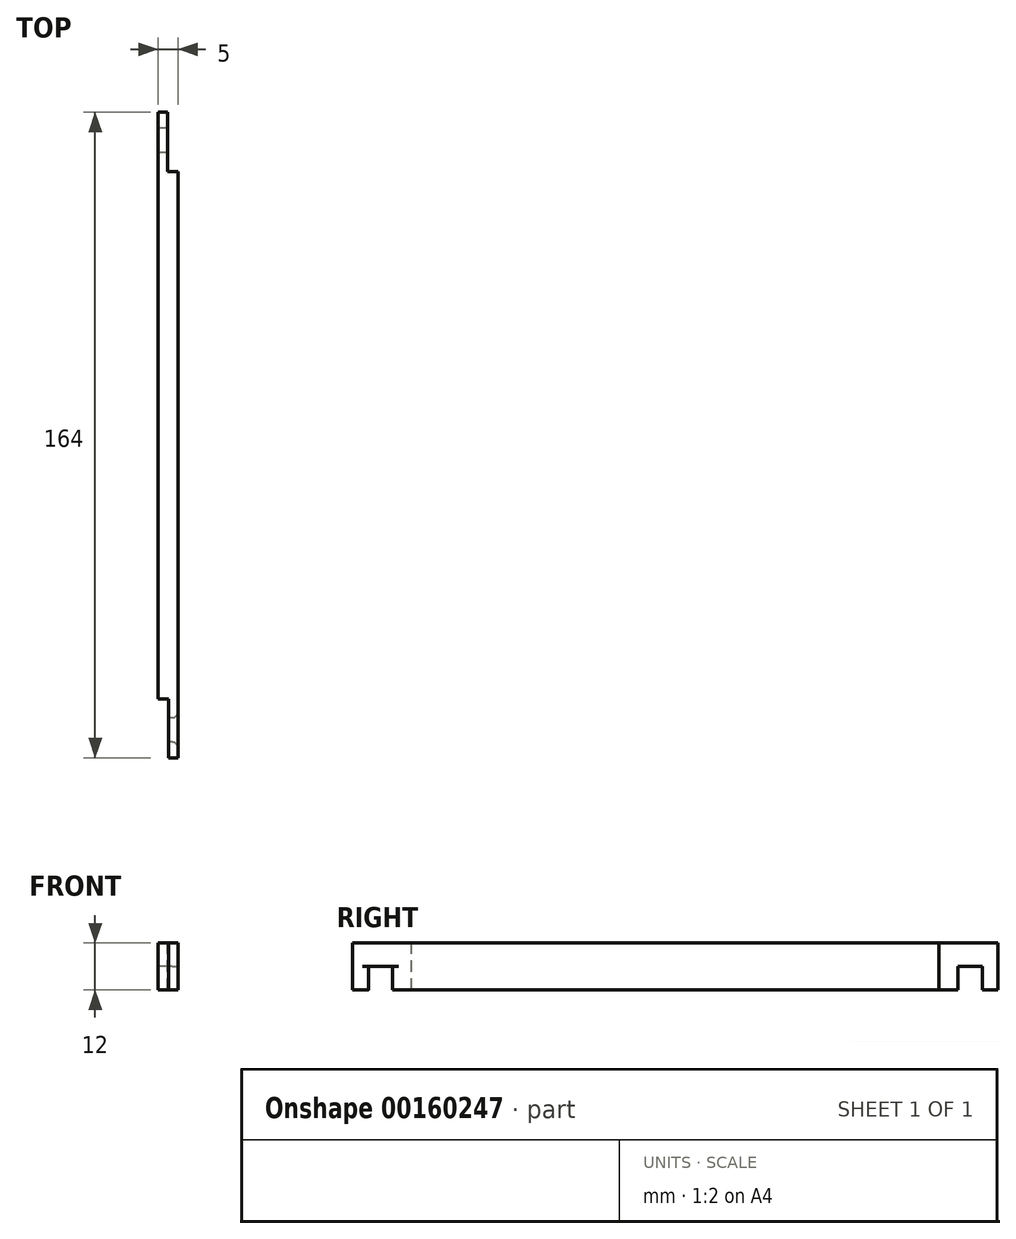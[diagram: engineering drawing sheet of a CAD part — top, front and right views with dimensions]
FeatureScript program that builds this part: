
annotation { "Feature Type Name" : "Feature", "Feature Type Description" : "" }
export const myFeature = defineFeature(function(context is Context, id is Id, definition is map)
    precondition{}
    {
        {
            var Q0;
            Q0=qCreatedBy(makeId("Right.planeOp"),FACE);
            var sketch = newSketch(context, id + "F0", { "sketchPlane" : qUnion([Q0])});
            skLineSegment(sketch, "E0.bottom", {"start": v(-59.21, 0) * mm, "end": v(104.79, 0) * mm});
            skLineSegment(sketch, "E0.top", {"start": v(-59.21, 12) * mm, "end": v(104.79, 12) * mm});
            skLineSegment(sketch, "E0.left", {"start": v(-59.21, 0) * mm, "end": v(-59.21, 12) * mm});
            skLineSegment(sketch, "E0.right", {"start": v(104.79, 0) * mm, "end": v(104.79, 12) * mm});
            skLineSegment(sketch, "E1.bottom", {"start": v(-55.21, 0) * mm, "end": v(-49.01, 0) * mm});
            skLineSegment(sketch, "E1.top", {"start": v(-55.21, 6) * mm, "end": v(-49.01, 6) * mm});
            skLineSegment(sketch, "E1.left", {"start": v(-55.21, 0) * mm, "end": v(-55.21, 6) * mm});
            skLineSegment(sketch, "E1.right", {"start": v(-49.01, 0) * mm, "end": v(-49.01, 6) * mm});
            skLineSegment(sketch, "E2.bottom", {"start": v(100.79, 0) * mm, "end": v(94.59, 0) * mm});
            skLineSegment(sketch, "E2.top", {"start": v(100.79, 6) * mm, "end": v(94.59, 6) * mm});
            skLineSegment(sketch, "E2.left", {"start": v(100.79, 0) * mm, "end": v(100.79, 6) * mm});
            skLineSegment(sketch, "E2.right", {"start": v(94.59, 0) * mm, "end": v(94.59, 6) * mm});
            skSolve(sketch);
        }
        {
            var Q0;
            Q0=makeQuery(id+"F0.imprint","IMPRINT",FACE,{"disambiguationData":[TD([[makeQuery(id+"F0.imprint","IMPRINT",EDGE,{"derivedFrom":sQuery(id+"F0.wireOp",EDGE,"E0.top")}),-1.0]])]});
            extrude(context, id + "F1", {"entities" : qUnion([Q0]), "depth" : 5 * mm});
        }
        {
            var Q0;
            Q0=makeQuery(id+"F1.opExtrude","CAP_EDGE",EDGE,{"disambiguationData":[OSD([sQuery(id+"F0.wireOp",EDGE,"E1.left")])],"isStart":false});
            var Q1;
            Q1=makeQuery(id+"F1.opExtrude","CAP_EDGE",EDGE,{"disambiguationData":[OSD([sQuery(id+"F0.wireOp",EDGE,"E1.right")])],"isStart":false});
            fillet(context, id + "F2", {"entities" : qUnion([Q0, Q1]), "radius" : 1.5 * mm, "tangentPropagation" : true, "allowEdgeOverflow" : false});
        }
        {
            var Q0;
            Q0=makeQuery(id+"F1.opExtrude","SWEPT_FACE",FACE,{"disambiguationData":[OSD([sQuery(id+"F0.wireOp",EDGE,"E0.top")])]});
            var sketch = newSketch(context, id + "F3", { "sketchPlane" : qUnion([Q0])});
            skLineSegment(sketch, "E3.bottom", {"start": v(0, -44.21) * mm, "end": v(2.6, -44.21) * mm});
            skLineSegment(sketch, "E3.top", {"start": v(0, -59.21) * mm, "end": v(2.6, -59.21) * mm});
            skLineSegment(sketch, "E3.left", {"start": v(0, -44.21) * mm, "end": v(0, -59.21) * mm});
            skLineSegment(sketch, "E3.right", {"start": v(2.6, -44.21) * mm, "end": v(2.6, -59.21) * mm});
            skLineSegment(sketch, "E4.bottom", {"start": v(5, 104.79) * mm, "end": v(2.4, 104.79) * mm});
            skLineSegment(sketch, "E4.top", {"start": v(5, 89.79) * mm, "end": v(2.4, 89.79) * mm});
            skLineSegment(sketch, "E4.left", {"start": v(5, 104.79) * mm, "end": v(5, 89.79) * mm});
            skLineSegment(sketch, "E4.right", {"start": v(2.4, 104.79) * mm, "end": v(2.4, 89.79) * mm});
            skSolve(sketch);
        }
        {
            var Q0;
            Q0=makeQuery(id+"F3.imprint","IMPRINT",FACE,{"disambiguationData":[TD([[makeQuery(id+"F3.imprint","IMPRINT",EDGE,{"derivedFrom":sQuery(id+"F3.wireOp",EDGE,"E4.bottom")}),1.0]])]});
            var Q1;
            Q1=makeQuery(id+"F3.imprint","IMPRINT",FACE,{"disambiguationData":[TD([[makeQuery(id+"F3.imprint","IMPRINT",EDGE,{"derivedFrom":sQuery(id+"F3.wireOp",EDGE,"E3.bottom")}),-1.0]])]});
            extrude(context, id + "F4", {"entities" : qUnion([Q0, Q1]), "operationType" : NewBodyOperationType.REMOVE, "endBound" : BoundingType.THROUGH_ALL, "oppositeDirection" : true, "depth" : 25 * mm});
        }
    });
